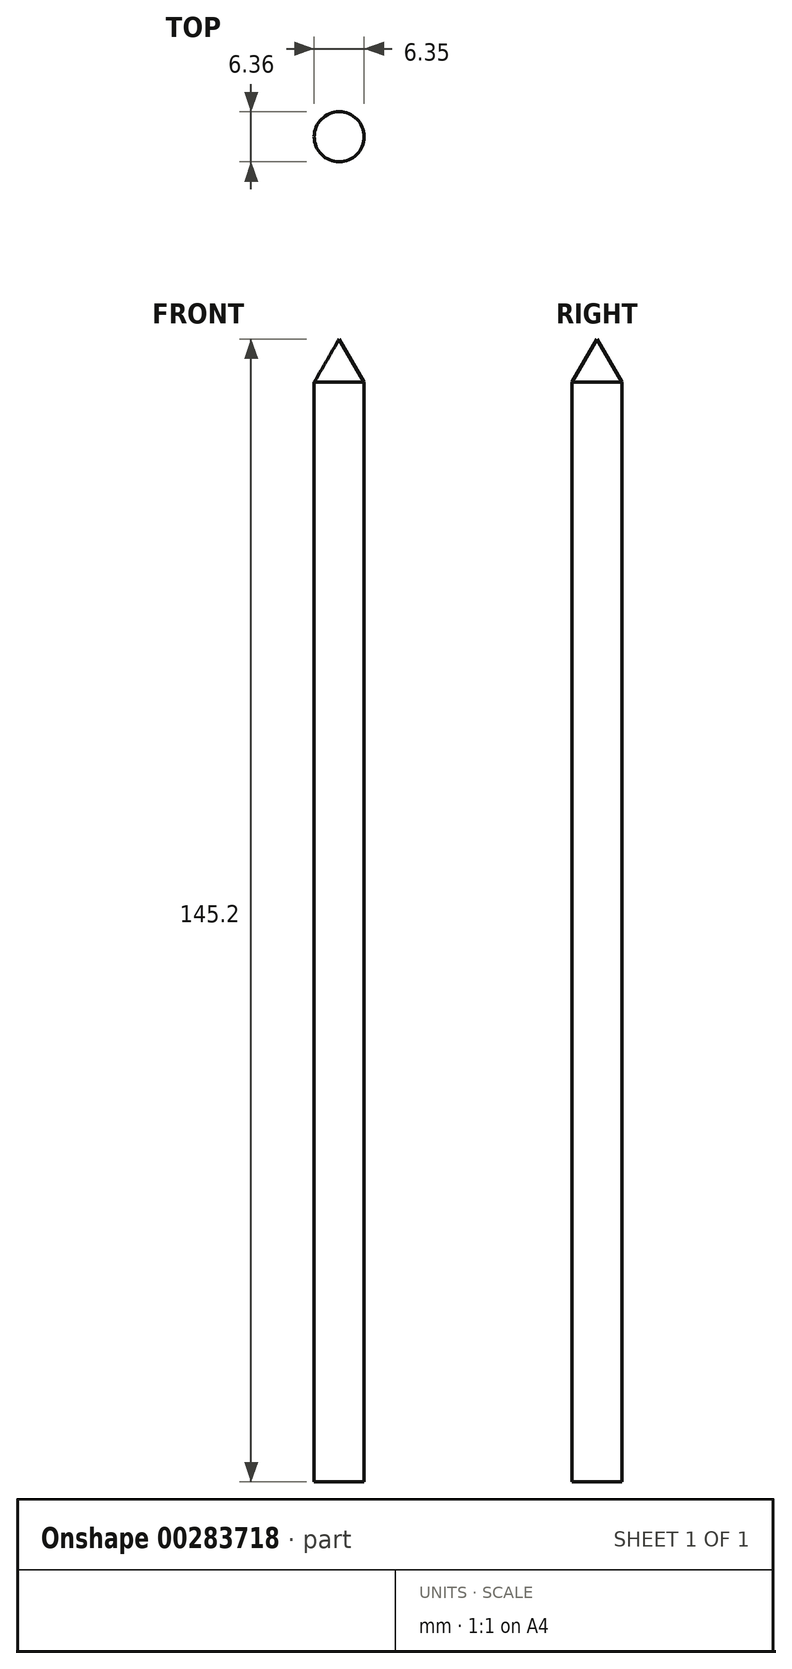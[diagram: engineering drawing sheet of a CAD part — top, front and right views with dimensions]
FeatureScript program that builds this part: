
annotation { "Feature Type Name" : "Feature", "Feature Type Description" : "" }
export const myFeature = defineFeature(function(context is Context, id is Id, definition is map)
    precondition{}
    {
        {
            var Q0;
            Q0=qCreatedBy(makeId("Front.planeOp"),FACE);
            var sketch = newSketch(context, id + "F0", { "sketchPlane" : qUnion([Q0])});
            skLineSegment(sketch, "E0.bottom", {"start": v(23.46, 92.12) * mm, "end": v(29.8, 92.12) * mm});
            skLineSegment(sketch, "E0.top", {"start": v(23.46, -47.58) * mm, "end": v(29.8, -47.58) * mm});
            skLineSegment(sketch, "E0.left", {"start": v(23.46, 92.12) * mm, "end": v(23.46, -47.58) * mm});
            skLineSegment(sketch, "E0.right", {"start": v(29.8, 92.12) * mm, "end": v(29.8, -47.58) * mm});
            skPoint(sketch, "E1.cCircle.centerSnap0", {"position": v(26.63, 92.12) * mm});
            skLineSegment(sketch, "E1.0", {"start": v(29.8, 92.12) * mm, "end": v(23.46, 92.12) * mm});
            skLineSegment(sketch, "E1.1", {"start": v(23.46, 92.12) * mm, "end": v(26.63, 97.62) * mm});
            skLineSegment(sketch, "E1.2", {"start": v(26.63, 97.62) * mm, "end": v(29.8, 92.12) * mm});
            skPoint(sketch, "E1.0.midPoint", {"position": v(26.63, 92.12) * mm});
            skPoint(sketch, "E1.cCircle.center.orphan", {"position": v(26.63, 93.95) * mm});
            skLineSegment(sketch, "E2", {"start": v(26.63, 97.62) * mm, "end": v(26.63, -47.58) * mm});
            skSolve(sketch);
        }
        {
            var Q0;
            {var subQ0=sQuery(id+"F0.wireOp",EDGE,"E1.2");Q0=makeQuery(id+"F0.imprint","IMPRINT",FACE,{"disambiguationData":[TD([[makeQuery(id+"F0.imprint","IMPRINT",EDGE,{"derivedFrom":subQ0}),-1.0]])]});}
            var Q1;
            {var subQ0=sQuery(id+"F0.wireOp",EDGE,"E0.right");Q1=makeQuery(id+"F0.imprint","IMPRINT",FACE,{"disambiguationData":[TD([[makeQuery(id+"F0.imprint","IMPRINT",EDGE,{"derivedFrom":subQ0}),-1.0]])]});}
            var Q2;
            Q2=sQuery(id+"F0.wireOp",EDGE,"E2");
            revolve(context, id + "F1", {"entities" : qUnion([Q0, Q1]), "axis" : qUnion([Q2]), "revolveType" : RevolveType.FULL});
        }
    });
